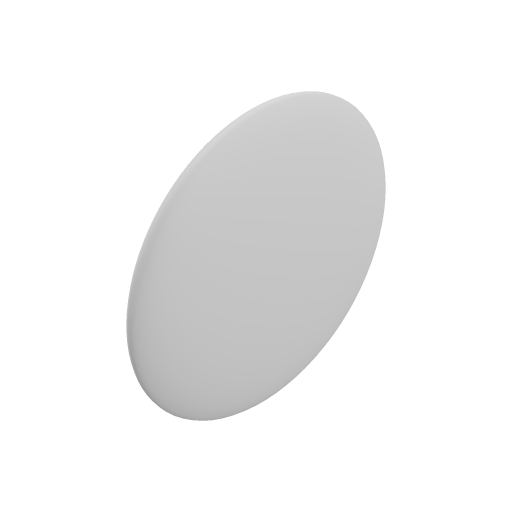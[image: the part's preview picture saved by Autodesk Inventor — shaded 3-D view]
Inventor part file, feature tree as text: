
AUTODESK INVENTOR PART (.ipt)
format: ipt  version: 2023 (Build 270158000, 158)  size: 157,184 bytes
history: native  units: in
note: dims shown in document units (in); Inventor stores cm internally (conversion verified against a paired STEP export)
features: revolve x1, sketch x1
ambient origin geometry x8: Origin, YZ Plane, XZ Plane, XY Plane, X Axis, Y Axis, Z Axis, Center Point
bodies: Solid1 (feature_tree)
feature tree (2):
  revolve  "Revolution1"  [1 undecoded]
  sketch  "Sketch1"  dims[d0=7.874in d1=39.3701in d2=90.0deg]
note: 1 required parameter value undecoded (feature->parameter linkage not recoverable at this tier; creation-order binding heuristic only, values carry confidence <= 0.55)
